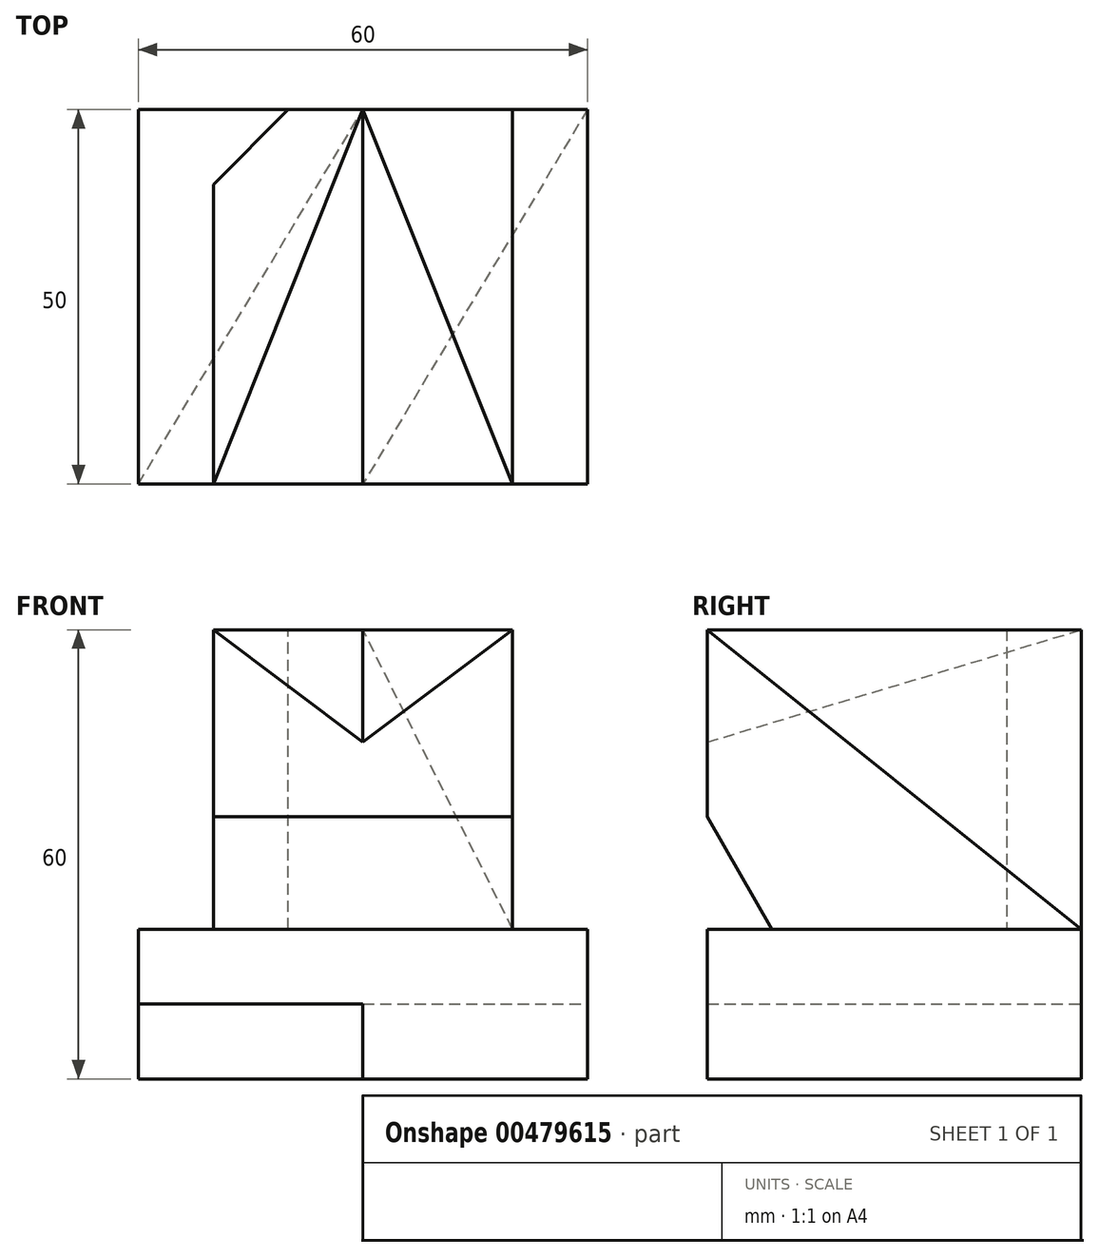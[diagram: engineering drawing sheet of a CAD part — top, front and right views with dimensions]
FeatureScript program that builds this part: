
annotation { "Feature Type Name" : "Feature", "Feature Type Description" : "" }
export const myFeature = defineFeature(function(context is Context, id is Id, definition is map)
    precondition{}
    {
        {
            var Q0;
            Q0=qCreatedBy(makeId("Top.planeOp"),FACE);
            var sketch = newSketch(context, id + "F0", { "sketchPlane" : qUnion([Q0])});
            skLineSegment(sketch, "E0.bottom", {"start": v(0, 0) * mm, "end": v(60, 0) * mm});
            skLineSegment(sketch, "E0.top", {"start": v(0, 50) * mm, "end": v(60, 50) * mm});
            skLineSegment(sketch, "E0.left", {"start": v(0, 0) * mm, "end": v(0, 50) * mm});
            skLineSegment(sketch, "E0.right", {"start": v(60, 0) * mm, "end": v(60, 50) * mm});
            skSolve(sketch);
        }
        {
            var Q0;
            Q0 = qSketchRegion(id + "F0", true);
            extrude(context, id + "F1", {"entities" : qUnion([Q0]), "depth" : 60 * mm, "offsetDistance" : 25 * mm});
        }
        {
            var Q0;
            Q0=makeQuery(id+"F1.opExtrude","SWEPT_FACE",FACE,{"disambiguationData":[OSD([sQuery(id+"F0.wireOp",EDGE,"E0.bottom")])]});
            var sketch = newSketch(context, id + "F2", { "sketchPlane" : qUnion([Q0])});
            skLineSegment(sketch, "E1", {"start": v(0, 20) * mm, "end": v(10, 20) * mm});
            skLineSegment(sketch, "E2", {"start": v(10, 20) * mm, "end": v(10, 60) * mm});
            skLineSegment(sketch, "E3", {"start": v(10, 60) * mm, "end": v(50, 60) * mm});
            skLineSegment(sketch, "E4", {"start": v(50, 60) * mm, "end": v(50, 20) * mm});
            skLineSegment(sketch, "E5", {"start": v(50, 20) * mm, "end": v(60, 20) * mm});
            skSolve(sketch);
        }
        {
            var Q0;
            Q0 = qSketchRegion(id + "F2", true);
            var Q1;
            {var subQ0=sQuery(id+"F2.wireOp",EDGE,"E1");Q1=makeQuery(id+"F2.imprint","IMPRINT",FACE,{"disambiguationData":[TD([[makeQuery(id+"F2.imprint","IMPRINT",EDGE,{"derivedFrom":subQ0}),1.0]])]});}
            var Q2;
            {var subQ0=sQuery(id+"F2.wireOp",EDGE,"E4");Q2=makeQuery(id+"F2.imprint","IMPRINT",FACE,{"disambiguationData":[TD([[makeQuery(id+"F2.imprint","IMPRINT",EDGE,{"derivedFrom":subQ0}),1.0]])]});}
            extrude(context, id + "F3", {"entities" : qUnion([Q0, Q1, Q2]), "operationType" : NewBodyOperationType.REMOVE, "endBound" : BoundingType.THROUGH_ALL, "oppositeDirection" : true, "depth" : 25 * mm, "offsetDistance" : 25 * mm});
        }
        {
            var Q0;
            Q0=makeQuery(id+"F3.boolean.opBoolean","COPY",FACE,{"derivedFrom":makeQuery(id+"F3.opExtrude","SWEPT_FACE",FACE,{"disambiguationData":[OSD([sQuery(id+"F2.wireOp",EDGE,"E4")])]})});
            var sketch = newSketch(context, id + "F4", { "sketchPlane" : qUnion([Q0])});
            skLineSegment(sketch, "E6", {"start": v(0, 35) * mm, "end": v(8.66, 20) * mm});
            skLineSegment(sketch, "E7", {"start": v(8.66, 20) * mm, "end": v(0, 20) * mm});
            skLineSegment(sketch, "E8", {"start": v(0, 20) * mm, "end": v(0, 35) * mm});
            skSolve(sketch);
        }
        {
            var Q0;
            Q0 = qSketchRegion(id + "F4", true);
            extrude(context, id + "F5", {"entities" : qUnion([Q0]), "operationType" : NewBodyOperationType.REMOVE, "endBound" : BoundingType.THROUGH_ALL, "oppositeDirection" : true, "depth" : 25 * mm, "offsetDistance" : 25 * mm});
        }
        {
            var Q0;
            Q0=makeQuery(id+"F1.opExtrude","CAP_FACE",FACE,{"disambiguationData":[OSD([sQuery(id+"F0.wireOp",EDGE,"E0.bottom"),sQuery(id+"F0.wireOp",EDGE,"E0.top"),sQuery(id+"F0.wireOp",EDGE,"E0.left"),sQuery(id+"F0.wireOp",EDGE,"E0.right")])],"isStart":true});
            var sketch = newSketch(context, id + "F6", { "sketchPlane" : qUnion([Q0])});
            skLineSegment(sketch, "E9", {"start": v(0, 0) * mm, "end": v(30, -50) * mm});
            skLineSegment(sketch, "E10", {"start": v(60, -50) * mm, "end": v(30, 0) * mm});
            skLineSegment(sketch, "E11", {"start": v(30, 0) * mm, "end": v(0, 0) * mm});
            skSolve(sketch);
        }
        {
            var Q0;
            Q0 = qSketchRegion(id + "F6", true);
            var Q1;
            {var subQ0=sQuery(id+"F6.wireOp",EDGE,"E9");Q1=makeQuery(id+"F6.imprint","IMPRINT",FACE,{"disambiguationData":[TD([[makeQuery(id+"F6.imprint","IMPRINT",EDGE,{"derivedFrom":subQ0}),1.0]])]});}
            extrude(context, id + "F7", {"entities" : qUnion([Q0, Q1]), "operationType" : NewBodyOperationType.REMOVE, "oppositeDirection" : true, "depth" : 10 * mm, "offsetDistance" : 25 * mm});
        }
        {
            var Q0;
            {var subQ0=sQuery(id+"F0.wireOp",EDGE,"E0.bottom");Q0=makeQuery(id+"F5.boolean.opBoolean","SPLIT",FACE,{"disambiguationData":[TD([makeQuery(id+"F3.boolean.opBoolean","COPY",FACE,{"derivedFrom":makeQuery(id+"F3.opExtrude","SWEPT_FACE",FACE,{"disambiguationData":[OSD([sQuery(id+"F2.wireOp",EDGE,"E2")])]})})])],"derivedFrom":makeQuery(id+"F1.opExtrude","SWEPT_FACE",FACE,{"disambiguationData":[OSD([subQ0])]})});}
            var sketch = newSketch(context, id + "F8", { "sketchPlane" : qUnion([Q0])});
            skLineSegment(sketch, "E12", {"start": v(10, 60) * mm, "end": v(30, 45) * mm});
            skLineSegment(sketch, "E13", {"start": v(30, 45) * mm, "end": v(50, 60) * mm});
            skSolve(sketch);
        }
        {
            var Q0;
            Q0=makeQuery(id+"F3.boolean.opBoolean","COPY",FACE,{"derivedFrom":makeQuery(id+"F3.opExtrude","SWEPT_FACE",FACE,{"disambiguationData":[OSD([sQuery(id+"F2.wireOp",EDGE,"E4")])]})});
            var sketch = newSketch(context, id + "F9", { "sketchPlane" : qUnion([Q0])});
            skLineSegment(sketch, "E14", {"start": v(0, 45) * mm, "end": v(50, 60) * mm});
            skSolve(sketch);
        }
        {
            var Q0;
            Q0=makeQuery(id+"F8.imprint","IMPRINT",FACE,{"disambiguationData":[TD([[makeQuery(id+"F8.imprint","IMPRINT",EDGE,{"derivedFrom":sQuery(id+"F8.wireOp",EDGE,"E12")}),1.0]])]});
            var Q1;
            Q1=sQuery(id+"F9.wireOp",EDGE,"E14");
            sweep(context, id + "F10", {"operationType" : NewBodyOperationType.REMOVE, "profiles" : qUnion([Q0]), "path" : qUnion([Q1])});
        }
        {
            var Q0;
            Q0=makeQuery(id+"F3.boolean.opBoolean","INTERSECT",EDGE,{"derivedFrom":[makeQuery(id+"F1.opExtrude","SWEPT_FACE",FACE,{"disambiguationData":[OSD([sQuery(id+"F0.wireOp",EDGE,"E0.top")])]}),makeQuery(id+"F3.opExtrude","SWEPT_FACE",FACE,{"disambiguationData":[OSD([sQuery(id+"F2.wireOp",EDGE,"E2")])]})]});
            chamfer(context, id + "F11", {"entities" : qUnion([Q0]), "width" : 10 * mm, "tangentPropagation" : true});
        }
        {
            var Q0;
            Q0=makeQuery(id+"F3.boolean.opBoolean","COPY",FACE,{"derivedFrom":makeQuery(id+"F3.opExtrude","SWEPT_FACE",FACE,{"disambiguationData":[OSD([sQuery(id+"F2.wireOp",EDGE,"E4")])]})});
            var sketch = newSketch(context, id + "F12", { "sketchPlane" : qUnion([Q0])});
            skLineSegment(sketch, "E15", {"start": v(0, 60) * mm, "end": v(50, 20) * mm});
            skSolve(sketch);
        }
        {
            var Q0;
            {var subQ0=sQuery(id+"F0.wireOp",EDGE,"E0.top");var subQ1=sQuery(id+"F0.wireOp",EDGE,"E0.bottom");var subQ2=makeQuery(id+"F1.opExtrude","CAP_FACE",FACE,{"disambiguationData":[OSD([subQ1,subQ0,sQuery(id+"F0.wireOp",EDGE,"E0.left"),sQuery(id+"F0.wireOp",EDGE,"E0.right")])],"isStart":false});Q0=makeQuery(id+"F10.boolean.opBoolean","SPLIT",FACE,{"disambiguationData":[TD([makeQuery(id+"F3.boolean.opBoolean","COPY",FACE,{"derivedFrom":makeQuery(id+"F3.opExtrude","SWEPT_FACE",FACE,{"disambiguationData":[OSD([sQuery(id+"F2.wireOp",EDGE,"E4")])]})})])],"derivedFrom":subQ2});}
            var Q1;
            Q1=sQuery(id+"F12.wireOp",EDGE,"E15");
            sweep(context, id + "F13", {"operationType" : NewBodyOperationType.REMOVE, "profiles" : qUnion([Q0]), "path" : qUnion([Q1])});
        }
    });
